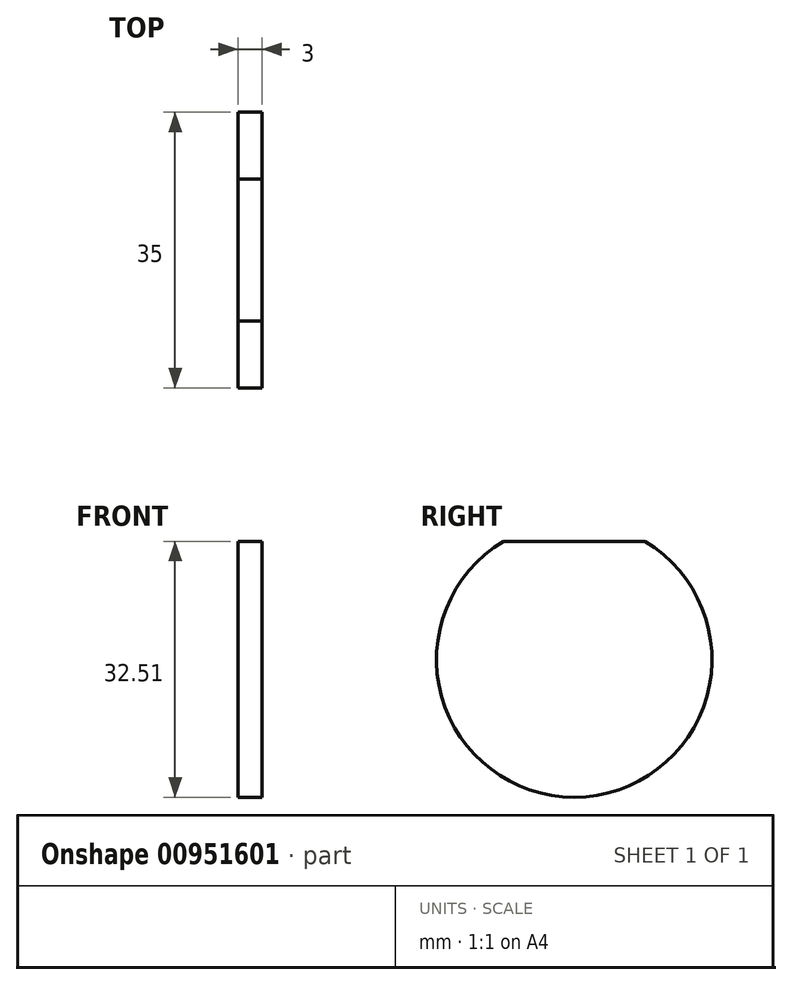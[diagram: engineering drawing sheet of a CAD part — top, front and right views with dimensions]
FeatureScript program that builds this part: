
annotation { "Feature Type Name" : "Feature", "Feature Type Description" : "" }
export const myFeature = defineFeature(function(context is Context, id is Id, definition is map)
    precondition{}
    {
        {
            var Q0;
            Q0=qCreatedBy(makeId("Right.planeOp"),FACE);
            var sketch = newSketch(context, id + "F0", { "sketchPlane" : qUnion([Q0])});
            skPoint(sketch, "E0", {"position": v(-9, 15) * mm});
            skPoint(sketch, "E1", {"position": v(9, 15) * mm});
            skLineSegment(sketch, "E2", {"start": v(-9, 15) * mm, "end": v(9, 15) * mm});
            skArc(sketch, "E3", {"start": v(-9, 15) * mm, "mid": v(0, -17.5) * mm, "end": v(9, 15) * mm});
            skLineSegment(sketch, "E4", {"start": v(0, 15) * mm, "end": v(0, 0) * mm, "construction": true});
            skCircle(sketch, "E5", {"center": v(0, 0) * mm, "radius": 6.25 * mm, "construction": true});
            skSolve(sketch);
        }
        {
            var Q0;
            Q0=qSketchRegion(id+"F0",true);
            extrude(context, id + "F1", {"entities" : qUnion([Q0]), "depth" : 3 * mm, "offsetDistance" : 25 * mm});
        }
    });
